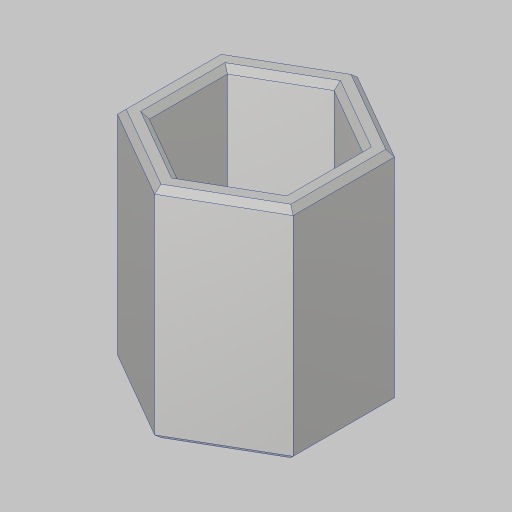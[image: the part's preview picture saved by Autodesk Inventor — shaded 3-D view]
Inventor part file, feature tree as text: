
AUTODESK INVENTOR PART (.ipt)
format: ipt  version: 2023.5 (Build 275446000, 446)  size: 129,536 bytes
history: native  units: in
note: dims shown in document units (in); Inventor stores cm internally (conversion verified against a paired STEP export)
features: extrude x1, chamfer x1, sketch x1
ambient origin geometry x8: Origin, YZ Plane, XZ Plane, XY Plane, X Axis, Y Axis, Z Axis, Center Point
bodies: Solid1 (feature_tree)
feature tree (3):
  extrude  "Extrusion1"  Depth=0.5in
  chamfer  "Chamfer1"  Distance=0.625in
  sketch  "Sketch1"  dims[d0=0.385in d1=0.5in d2=0.625in d3=0.0in d4=0.0157in d5=0.125in d6=45.0deg]
